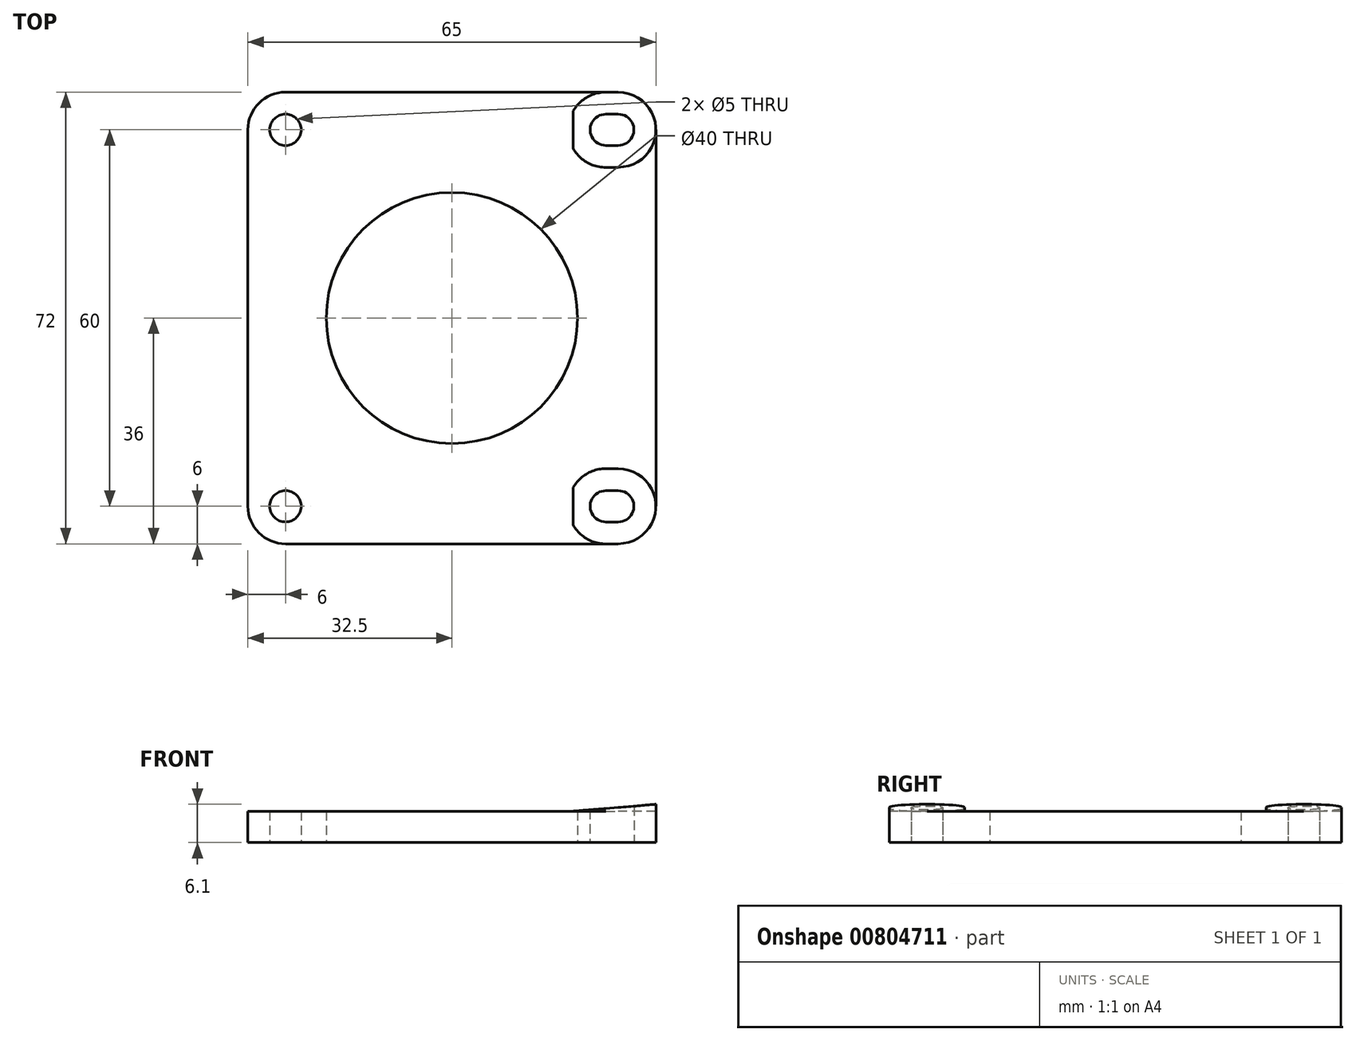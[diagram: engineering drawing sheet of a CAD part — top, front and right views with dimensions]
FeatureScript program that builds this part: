
annotation { "Feature Type Name" : "Feature", "Feature Type Description" : "" }
export const myFeature = defineFeature(function(context is Context, id is Id, definition is map)
    precondition{}
    {
        {
            var Q0;
            Q0=qCreatedBy(makeId("Top.planeOp"),FACE);
            var sketch = newSketch(context, id + "F0", { "sketchPlane" : qUnion([Q0])});
            skLineSegment(sketch, "E0.bottom", {"start": v(-32.5, -36) * mm, "end": v(32.5, -36) * mm});
            skLineSegment(sketch, "E0.top", {"start": v(-32.5, 36) * mm, "end": v(32.5, 36) * mm});
            skLineSegment(sketch, "E0.left", {"start": v(-32.5, -36) * mm, "end": v(-32.5, 36) * mm});
            skLineSegment(sketch, "E0.right", {"start": v(32.5, -36) * mm, "end": v(32.5, 36) * mm});
            skPoint(sketch, "E0.middle", {"position": v(0, 0) * mm});
            skCircle(sketch, "E1", {"center": v(0, 0) * mm, "radius": 20 * mm});
            skCircle(sketch, "E2", {"center": v(-26.5, 30) * mm, "radius": 2.5 * mm});
            skCircle(sketch, "E3", {"center": v(-26.5, -30) * mm, "radius": 2.5 * mm});
            skLineSegment(sketch, "E4", {"start": v(-26.5, -30) * mm, "end": v(-26.5, 30) * mm, "construction": true});
            skLineSegment(sketch, "E5", {"start": v(-26.5, 0) * mm, "end": v(0, 0) * mm, "construction": true});
            skLineSegment(sketch, "E6", {"start": v(24.5, -30) * mm, "end": v(26.5, -30) * mm, "construction": true});
            skLineSegment(sketch, "E7", {"start": v(24.5, 30) * mm, "end": v(26.5, 30) * mm, "construction": true});
            skArc(sketch, "E8.0.startCap", {"start": v(24.5, -32.5) * mm, "mid": v(22, -30) * mm, "end": v(24.5, -27.5) * mm});
            skArc(sketch, "E8.0.endCap", {"start": v(26.5, -27.5) * mm, "mid": v(29, -30) * mm, "end": v(26.5, -32.5) * mm});
            skLineSegment(sketch, "E8.0.left", {"start": v(24.5, -27.5) * mm, "end": v(26.5, -27.5) * mm});
            skLineSegment(sketch, "E8.0.right", {"start": v(24.5, -32.5) * mm, "end": v(26.5, -32.5) * mm});
            skArc(sketch, "E9.0.startCap", {"start": v(24.5, 27.5) * mm, "mid": v(22, 30) * mm, "end": v(24.5, 32.5) * mm});
            skArc(sketch, "E9.0.endCap", {"start": v(26.5, 32.5) * mm, "mid": v(29, 30) * mm, "end": v(26.5, 27.5) * mm});
            skLineSegment(sketch, "E9.0.left", {"start": v(24.5, 32.5) * mm, "end": v(26.5, 32.5) * mm});
            skLineSegment(sketch, "E9.0.right", {"start": v(24.5, 27.5) * mm, "end": v(26.5, 27.5) * mm});
            skSolve(sketch);
        }
        {
            var Q0;
            Q0=qSketchRegion(id+"F0",true);
            extrude(context, id + "F1", {"entities" : qUnion([Q0]), "depth" : 5 * mm, "offsetDistance" : 25 * mm});
        }
        {
            var Q0;
            Q0=makeQuery(id+"F1.opExtrude","CAP_FACE",FACE,{"disambiguationData":[OSD([sQuery(id+"F0.wireOp",EDGE,"E0.bottom"),sQuery(id+"F0.wireOp",EDGE,"E0.top"),sQuery(id+"F0.wireOp",EDGE,"E0.left"),sQuery(id+"F0.wireOp",EDGE,"E0.right"),sQuery(id+"F0.wireOp",EDGE,"E1"),sQuery(id+"F0.wireOp",EDGE,"E2"),sQuery(id+"F0.wireOp",EDGE,"E3"),sQuery(id+"F0.wireOp",EDGE,"E8.0.startCap"),sQuery(id+"F0.wireOp",EDGE,"E8.0.endCap"),sQuery(id+"F0.wireOp",EDGE,"E8.0.left"),sQuery(id+"F0.wireOp",EDGE,"E8.0.right"),sQuery(id+"F0.wireOp",EDGE,"E9.0.startCap"),sQuery(id+"F0.wireOp",EDGE,"E9.0.endCap"),sQuery(id+"F0.wireOp",EDGE,"E9.0.left"),sQuery(id+"F0.wireOp",EDGE,"E9.0.right")])],"isStart":false});
            var sketch = newSketch(context, id + "F2", { "sketchPlane" : qUnion([Q0])});
            skLineSegment(sketch, "E10.0", {"start": v(24.5, -24) * mm, "end": v(26.5, -24) * mm});
            skArc(sketch, "E10.1", {"start": v(24.5, -36) * mm, "mid": v(18.5, -30) * mm, "end": v(24.5, -24) * mm});
            skLineSegment(sketch, "E10.2", {"start": v(24.5, -36) * mm, "end": v(26.5, -36) * mm});
            skArc(sketch, "E10.3", {"start": v(26.5, -24) * mm, "mid": v(32.5, -30) * mm, "end": v(26.5, -36) * mm});
            skLineSegment(sketch, "E11.0", {"start": v(24.5, 24) * mm, "end": v(26.5, 24) * mm});
            skArc(sketch, "E11.1", {"start": v(24.5, 24) * mm, "mid": v(18.5, 30) * mm, "end": v(24.5, 36) * mm});
            skLineSegment(sketch, "E11.2", {"start": v(24.5, 36) * mm, "end": v(26.5, 36) * mm});
            skArc(sketch, "E11.3", {"start": v(26.5, 36) * mm, "mid": v(32.5, 30) * mm, "end": v(26.5, 24) * mm});
            skSolve(sketch);
        }
        {
            var Q0;
            {var subQ1=sQuery(id+"F2.wireOp",EDGE,"E10.0");Q0=makeQuery(id+"F2.imprint","IMPRINT",FACE,{"disambiguationData":[TD([[makeQuery(id+"F2.imprint","IMPRINT",EDGE,{"derivedFrom":subQ1}),-1.0]])]});}
            var Q1;
            {var subQ3=sQuery(id+"F2.wireOp",EDGE,"E11.0");Q1=makeQuery(id+"F2.imprint","IMPRINT",FACE,{"disambiguationData":[TD([[makeQuery(id+"F2.imprint","IMPRINT",EDGE,{"derivedFrom":subQ3}),1.0]])]});}
            extrude(context, id + "F3", {"entities" : qUnion([Q0, Q1]), "operationType" : NewBodyOperationType.ADD, "depth" : 1.1 * mm, "offsetDistance" : 25 * mm});
        }
        {
            var Q0;
            Q0=makeQuery(id+"F3.boolean.opBoolean","MERGE",FACE,{"derivedFrom":[makeQuery(id+"F1.opExtrude","SWEPT_FACE",FACE,{"disambiguationData":[OSD([sQuery(id+"F0.wireOp",EDGE,"E0.bottom")])]}),makeQuery(id+"F3.opExtrude","SWEPT_FACE",FACE,{"disambiguationData":[OSD([sQuery(id+"F2.wireOp",EDGE,"E10.2")])]})]});
            var sketch = newSketch(context, id + "F4", { "sketchPlane" : qUnion([Q0])});
            skLineSegment(sketch, "E12", {"start": v(32.5, 6.1) * mm, "end": v(19.3, 5) * mm});
            skLineSegment(sketch, "E13", {"start": v(18.5, 6.1) * mm, "end": v(32.5, 6.1) * mm});
            skLineSegment(sketch, "E14", {"start": v(18.5, 6.1) * mm, "end": v(18.5, 5) * mm});
            skLineSegment(sketch, "E15", {"start": v(18.5, 5) * mm, "end": v(19.3, 5) * mm});
            skSolve(sketch);
        }
        {
            var Q0;
            Q0=qSketchRegion(id+"F4",true);
            extrude(context, id + "F5", {"entities" : qUnion([Q0]), "operationType" : NewBodyOperationType.REMOVE, "endBound" : BoundingType.THROUGH_ALL, "oppositeDirection" : true, "depth" : 25 * mm, "offsetDistance" : 25 * mm});
        }
        {
            var Q0;
            Q0=makeQuery(id+"F1.opExtrude","SWEPT_EDGE",EDGE,{"disambiguationData":[OSD([sQuery(id+"F0.wireOp",EDGE,"E0.bottom"),sQuery(id+"F0.wireOp",EDGE,"E0.left")])]});
            var Q1;
            Q1=makeQuery(id+"F1.opExtrude","SWEPT_EDGE",EDGE,{"disambiguationData":[OSD([sQuery(id+"F0.wireOp",EDGE,"E0.top"),sQuery(id+"F0.wireOp",EDGE,"E0.left")])]});
            var Q2;
            Q2=makeQuery(id+"F1.opExtrude","SWEPT_EDGE",EDGE,{"disambiguationData":[OSD([sQuery(id+"F0.wireOp",EDGE,"E0.top"),sQuery(id+"F0.wireOp",EDGE,"E0.right")])]});
            var Q3;
            Q3=makeQuery(id+"F1.opExtrude","SWEPT_EDGE",EDGE,{"disambiguationData":[OSD([sQuery(id+"F0.wireOp",EDGE,"E0.bottom"),sQuery(id+"F0.wireOp",EDGE,"E0.right")])]});
            fillet(context, id + "F6", {"entities" : qUnion([Q0, Q1, Q2, Q3]), "radius" : 6 * mm, "tangentPropagation" : true, "allowEdgeOverflow" : false});
        }
    });
